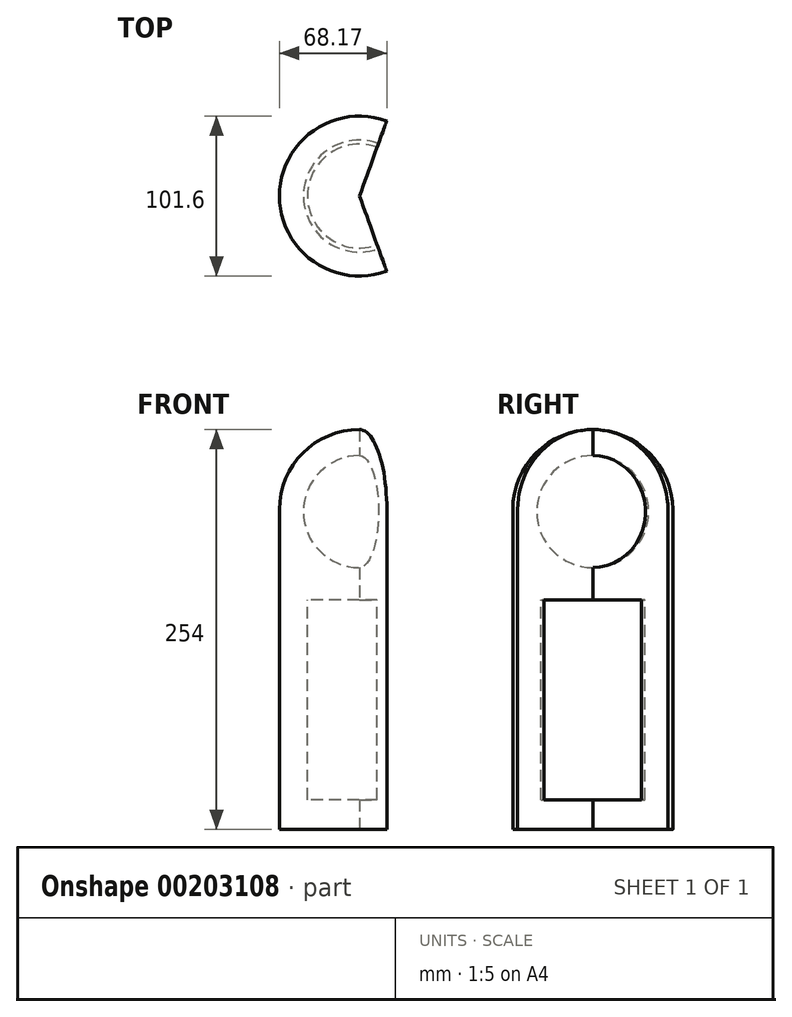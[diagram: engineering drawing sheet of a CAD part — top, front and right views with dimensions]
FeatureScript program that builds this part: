
annotation { "Feature Type Name" : "Feature", "Feature Type Description" : "" }
export const myFeature = defineFeature(function(context is Context, id is Id, definition is map)
    precondition{}
    {
        {
            var Q0;
            Q0=qCreatedBy(makeId("Front.planeOp"),FACE);
            var sketch = newSketch(context, id + "F0", { "sketchPlane" : qUnion([Q0])});
            skLineSegment(sketch, "E0", {"start": v(-50.8, 202.9) * mm, "end": v(-50.8, -0.3) * mm});
            skArc(sketch, "E1", {"start": v(0, 253.7) * mm, "mid": v(-35.92, 238.82) * mm, "end": v(-50.8, 202.9) * mm});
            skLineSegment(sketch, "E2", {"start": v(0, 253.7) * mm, "end": v(0, 0) * mm});
            skLineSegment(sketch, "E3", {"start": v(-50.8, -0.3) * mm, "end": v(0, 0) * mm});
            skLineSegment(sketch, "E4", {"start": v(0, 202.9) * mm, "end": v(0, 253.7) * mm});
            skLineSegment(sketch, "E5", {"start": v(0, 0) * mm, "end": v(0, 202.9) * mm});
            skSolve(sketch);
        }
        {
            var Q0;
            Q0 = qSketchRegion(id + "F0", true);
            var Q1;
            Q1 = qConstructionFilter(qBodyType(qCreatedBy(id + "F0" ,EDGE), BodyType.WIRE), ConstructionObject.NO);
            var Q2;
            Q2=sQuery(id+"F0.wireOp",EDGE,"E2");
            revolve(context, id + "F1", {"entities" : qUnion([Q0]), "surfaceEntities" : qUnion([Q1]), "axis" : qUnion([Q2]), "revolveType" : RevolveType.SYMMETRIC, "angle" : 220 * degree});
        }
        {
            var Q0;
            Q0=qCreatedBy(makeId("Front.planeOp"),FACE);
            var sketch = newSketch(context, id + "F2", { "sketchPlane" : qUnion([Q0])});
            skArc(sketch, "E6", {"start": v(0, 237.14) * mm, "mid": v(-35.56, 201.58) * mm, "end": v(0, 166.02) * mm});
            skLineSegment(sketch, "E7", {"start": v(0, 237.14) * mm, "end": v(0, 166.02) * mm});
            skSolve(sketch);
        }
        {
            var Q0;
            Q0 = qSketchRegion(id + "F2", true);
            var Q1;
            Q1=sQuery(id+"F2.wireOp",EDGE,"XFy2V0uE-yOY4-26vX-UVcA-KLJ8vrO13xKO");
            var Q2;
            Q2=makeQuery(id+"F1.opRevolve","CAP_EDGE",EDGE,{"disambiguationData":[OSD([sQuery(id+"F0.wireOp",EDGE,"E2")])],"isStart":true});
            revolve(context, id + "F3", {"operationType" : NewBodyOperationType.REMOVE, "entities" : qUnion([Q0]), "surfaceEntities" : qUnion([Q1]), "axis" : qUnion([Q2]), "revolveType" : RevolveType.SYMMETRIC, "angle" : 220 * degree});
        }
        {
            var Q0;
            Q0=qCreatedBy(makeId("Front.planeOp"),FACE);
            var sketch = newSketch(context, id + "F4", { "sketchPlane" : qUnion([Q0])});
            skLineSegment(sketch, "E8.bottom", {"start": v(0, 145.55) * mm, "end": v(-33.02, 145.55) * mm});
            skLineSegment(sketch, "E8.top", {"start": v(0, 18.55) * mm, "end": v(-33.02, 18.55) * mm});
            skLineSegment(sketch, "E8.left", {"start": v(0, 145.55) * mm, "end": v(0, 18.55) * mm});
            skLineSegment(sketch, "E8.right", {"start": v(-33.02, 145.55) * mm, "end": v(-33.02, 18.55) * mm});
            skSolve(sketch);
        }
        {
            var Q0;
            Q0 = qSketchRegion(id + "F4", true);
            var Q1;
            {var subQ0=sQuery(id+"F0.wireOp",EDGE,"E3");var subQ1=sQuery(id+"F0.wireOp",EDGE,"E2");Q1=makeQuery(id+"F3.boolean.opBoolean","SPLIT",EDGE,{"disambiguationData":[TD([makeQuery(id+"F1.opRevolve","SWEPT_FACE",FACE,{"disambiguationData":[OSD([subQ0])]})])],"derivedFrom":makeQuery(id+"F1.opRevolve","CAP_EDGE",EDGE,{"disambiguationData":[OSD([subQ1])],"isStart":true})});}
            revolve(context, id + "F5", {"operationType" : NewBodyOperationType.REMOVE, "entities" : qUnion([Q0]), "axis" : qUnion([Q1]), "revolveType" : RevolveType.FULL});
        }
    });
